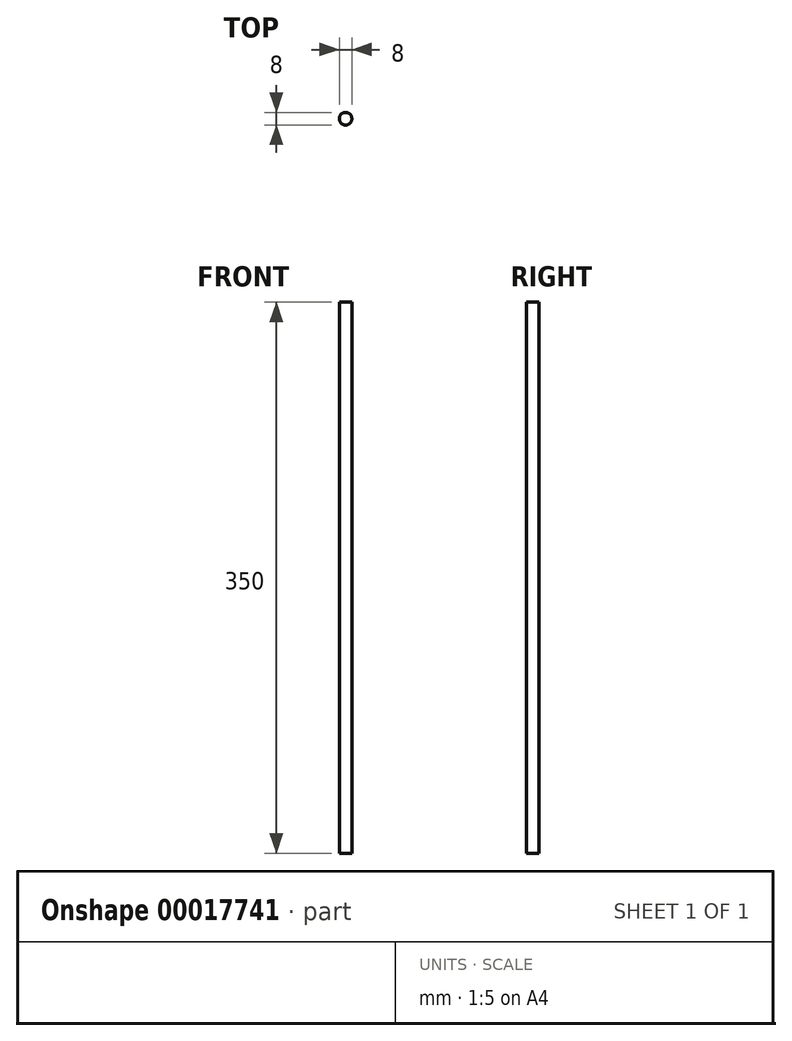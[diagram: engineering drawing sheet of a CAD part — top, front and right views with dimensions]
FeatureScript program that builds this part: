
annotation { "Feature Type Name" : "Feature", "Feature Type Description" : "" }
export const myFeature = defineFeature(function(context is Context, id is Id, definition is map)
    precondition{}
    {
        {
            var Q0;
            Q0=qCreatedBy(makeId("Top.planeOp"),FACE);
            var sketch = newSketch(context, id + "F0", { "sketchPlane" : qUnion([Q0])});
            skCircle(sketch, "E0", {"center": v(0, 0) * mm, "radius": 4 * mm});
            skSolve(sketch);
        }
        {
            var Q0;
            Q0=qSketchRegion(id+"F0",true);
            extrude(context, id + "F1", {"entities" : qUnion([Q0]), "depth" : 350 * mm});
        }
    });
